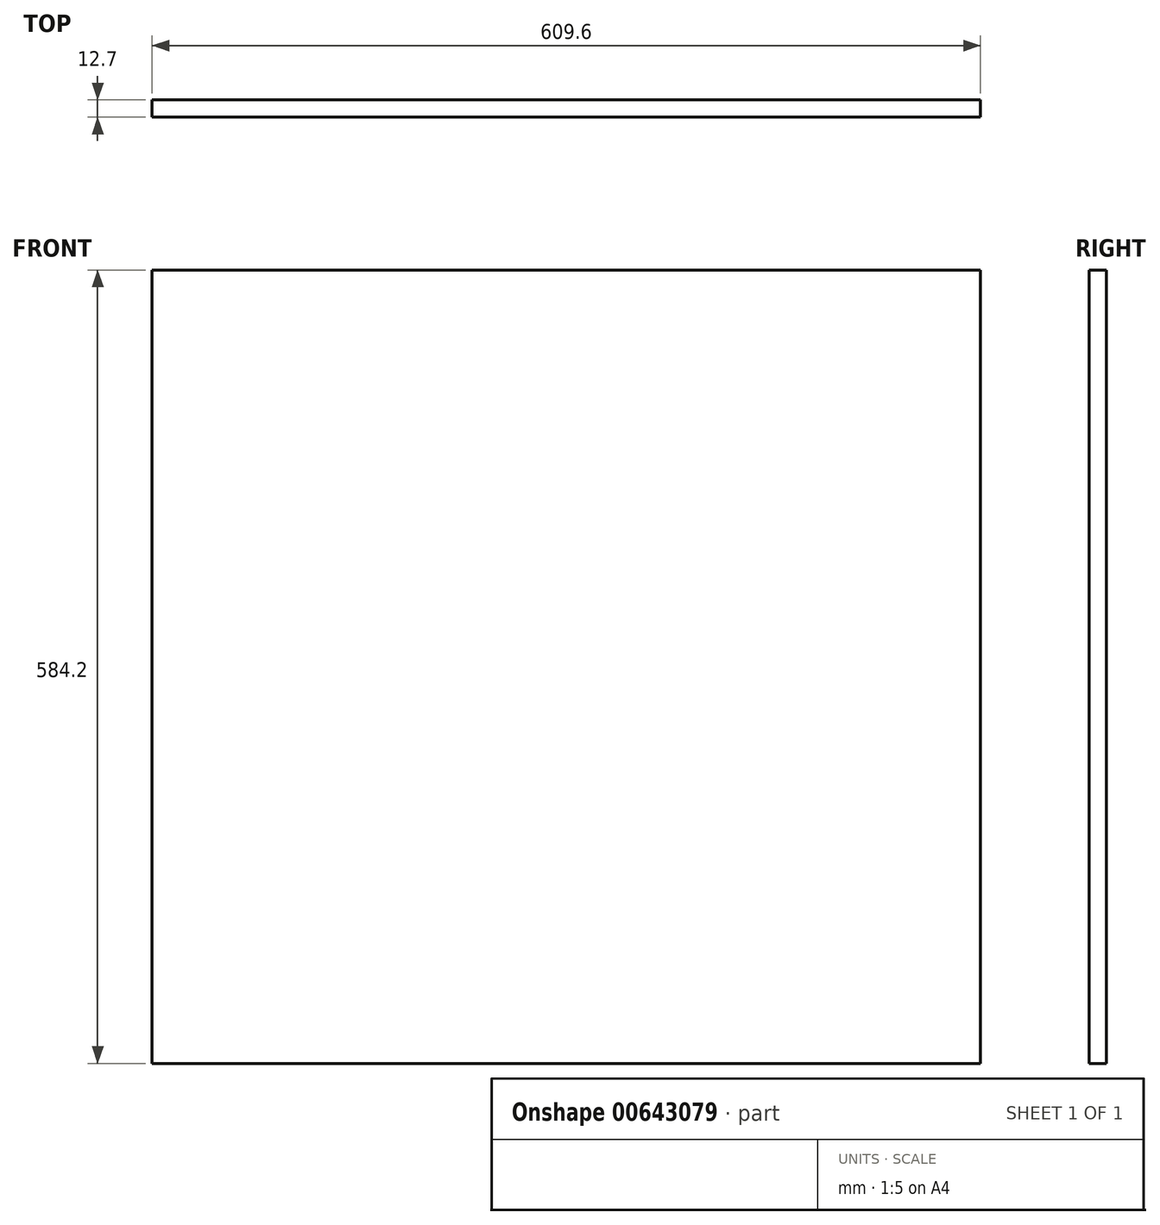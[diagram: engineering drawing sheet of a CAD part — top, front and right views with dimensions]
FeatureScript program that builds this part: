
annotation { "Feature Type Name" : "Feature", "Feature Type Description" : "" }
export const myFeature = defineFeature(function(context is Context, id is Id, definition is map)
    precondition{}
    {
        {
            var Q0;
            Q0=qCreatedBy(makeId("Front.planeOp"),FACE);
            var sketch = newSketch(context, id + "F0", { "sketchPlane" : qUnion([Q0])});
            skLineSegment(sketch, "E0.bottom", {"start": v(-39.48, 543.29) * mm, "end": v(570.12, 543.29) * mm});
            skLineSegment(sketch, "E0.top", {"start": v(-39.48, -40.91) * mm, "end": v(570.12, -40.91) * mm});
            skLineSegment(sketch, "E0.left", {"start": v(-39.48, 543.29) * mm, "end": v(-39.48, -40.91) * mm});
            skLineSegment(sketch, "E0.right", {"start": v(570.12, 543.29) * mm, "end": v(570.12, -40.91) * mm});
            skSolve(sketch);
        }
        {
            var Q0;
            Q0 = qSketchRegion(id + "F0", true);
            extrude(context, id + "F1", {"entities" : qUnion([Q0]), "depth" : 12.7 * mm, "offsetDistance" : 25.4 * mm});
        }
    });
